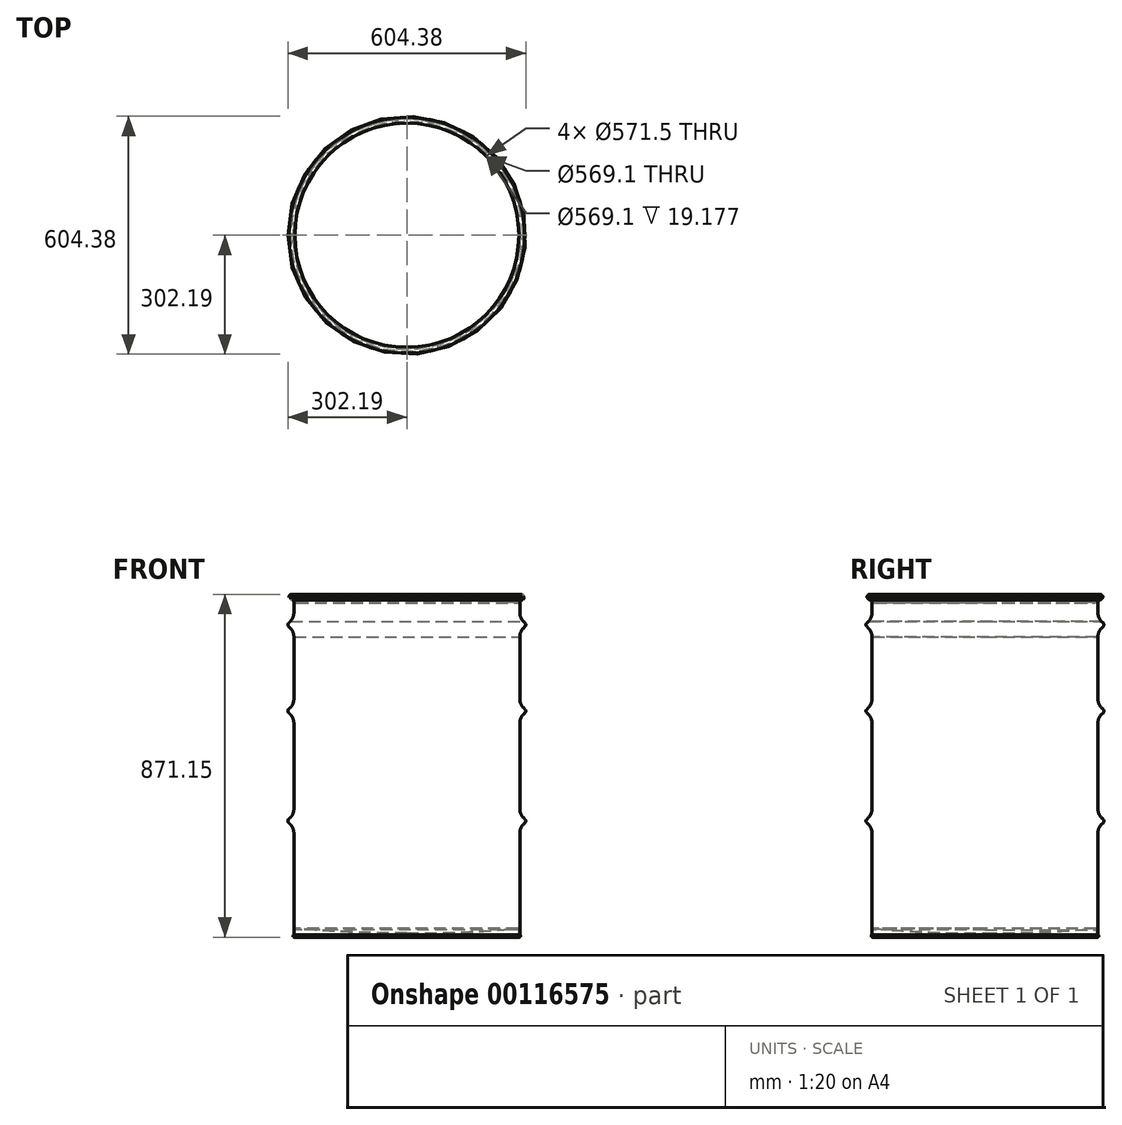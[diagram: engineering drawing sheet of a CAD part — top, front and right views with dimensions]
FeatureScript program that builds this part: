
annotation { "Feature Type Name" : "Feature", "Feature Type Description" : "" }
export const myFeature = defineFeature(function(context is Context, id is Id, definition is map)
    precondition{}
    {
        {
            var Q0;
            Q0=qCreatedBy(makeId("Front.planeOp"),FACE);
            var sketch = newSketch(context, id + "F0", { "sketchPlane" : qUnion([Q0])});
            skLineSegment(sketch, "E0.top", {"start": v(-286.95, 863.6) * mm, "end": v(-285.75, 863.6) * mm, "construction": true});
            skLineSegment(sketch, "E0.right", {"start": v(-285.75, 0) * mm, "end": v(-285.75, 264.7) * mm});
            skLineSegment(sketch, "E1", {"start": v(0, 0) * mm, "end": v(0, 177.34) * mm, "construction": true});
            skArc(sketch, "E2", {"start": v(-285.75, 863.6) * mm, "mid": v(-297.8, 866.42) * mm, "end": v(-288.25, 858.55) * mm});
            skArc(sketch, "E3", {"start": v(-286.95, 863.6) * mm, "mid": v(-296.72, 865.89) * mm, "end": v(-288.98, 859.5) * mm});
            skLineSegment(sketch, "E4", {"start": v(-288.98, 859.5) * mm, "end": v(-288.25, 858.55) * mm});
            skArc(sketch, "E5", {"start": v(-285.75, 0) * mm, "mid": v(-288.87, 2.56) * mm, "end": v(-286.95, 6.11) * mm});
            skLineSegment(sketch, "E6.trimOffspring", {"start": v(-286.95, 6.11) * mm, "end": v(-286.95, 264.7) * mm});
            skPoint(sketch, "E0.left.start.orphan", {"position": v(-286.95, 0) * mm});
            skLineSegment(sketch, "E7", {"start": v(-295.84, 802.73) * mm, "end": v(-300.33, 798.24) * mm});
            skLineSegment(sketch, "E8", {"start": v(-300.33, 789.26) * mm, "end": v(-295.84, 784.77) * mm});
            skLineSegment(sketch, "E9.trimOffspring", {"start": v(-286.95, 824.2) * mm, "end": v(-286.95, 863.6) * mm});
            skArc(sketch, "E10.filletArc", {"start": v(-300.33, 798.24) * mm, "mid": v(-302.2, 793.75) * mm, "end": v(-300.33, 789.26) * mm});
            skArc(sketch, "E11.filletArc", {"start": v(-295.84, 802.73) * mm, "mid": v(-289.26, 812.58) * mm, "end": v(-286.95, 824.2) * mm});
            skArc(sketch, "E12.filletArc", {"start": v(-286.95, 763.3) * mm, "mid": v(-289.26, 774.92) * mm, "end": v(-295.84, 784.77) * mm});
            skLineSegment(sketch, "E13", {"start": v(-302.19, 748.51) * mm, "end": v(-302.19, 170.1) * mm, "construction": true});
            skLineSegment(sketch, "E14", {"start": v(-292.1, 863.6) * mm, "end": v(-292.1, 869.95) * mm, "construction": true});
            skLineSegment(sketch, "E15", {"start": v(-300.33, 798.24) * mm, "end": v(-300.33, 789.26) * mm, "construction": true});
            skLineSegment(sketch, "E16", {"start": v(-295.84, 802.73) * mm, "end": v(-295.84, 784.77) * mm, "construction": true});
            skLineSegment(sketch, "E17", {"start": v(-286.95, 763.3) * mm, "end": v(-285.75, 763.3) * mm, "construction": true});
            skLineSegment(sketch, "E18", {"start": v(-286.95, 824.2) * mm, "end": v(-285.75, 824.2) * mm, "construction": true});
            skLineSegment(sketch, "E19.trimOffspring", {"start": v(-285.75, 824.2) * mm, "end": v(-285.75, 863.6) * mm});
            skLineSegment(sketch, "E20", {"start": v(-299.35, 790.24) * mm, "end": v(-294.86, 785.75) * mm});
            skLineSegment(sketch, "E21", {"start": v(-299.35, 797.26) * mm, "end": v(-294.86, 801.75) * mm});
            skArc(sketch, "E22", {"start": v(-299.35, 797.26) * mm, "mid": v(-300.8, 793.75) * mm, "end": v(-299.35, 790.24) * mm});
            skArc(sketch, "E23", {"start": v(-294.86, 801.75) * mm, "mid": v(-288.12, 812.08) * mm, "end": v(-285.75, 824.2) * mm});
            skArc(sketch, "E24", {"start": v(-285.75, 763.3) * mm, "mid": v(-288.03, 775.45) * mm, "end": v(-294.86, 785.75) * mm});
            skLineSegment(sketch, "E25", {"start": v(-295.84, 583.53) * mm, "end": v(-300.33, 579.04) * mm});
            skLineSegment(sketch, "E26", {"start": v(-300.33, 570.06) * mm, "end": v(-295.84, 565.57) * mm});
            skLineSegment(sketch, "E27.trimOffspring", {"start": v(-286.95, 605) * mm, "end": v(-286.95, 763.3) * mm});
            skPoint(sketch, "E28.visualSharp", {"position": v(-304.82, 574.55) * mm});
            skArc(sketch, "E28.filletArc", {"start": v(-300.33, 579.04) * mm, "mid": v(-302.2, 574.55) * mm, "end": v(-300.33, 570.06) * mm});
            skArc(sketch, "E29.filletArc", {"start": v(-295.84, 583.53) * mm, "mid": v(-289.26, 593.38) * mm, "end": v(-286.95, 605) * mm});
            skArc(sketch, "E30.filletArc", {"start": v(-286.95, 544.1) * mm, "mid": v(-289.26, 555.72) * mm, "end": v(-295.84, 565.57) * mm});
            skLineSegment(sketch, "E31", {"start": v(-295.84, 583.53) * mm, "end": v(-295.84, 565.57) * mm, "construction": true});
            skLineSegment(sketch, "E32", {"start": v(-286.95, 544.1) * mm, "end": v(-285.75, 544.1) * mm, "construction": true});
            skLineSegment(sketch, "E33", {"start": v(-286.95, 605) * mm, "end": v(-285.75, 605) * mm, "construction": true});
            skLineSegment(sketch, "E34.trimOffspring", {"start": v(-285.75, 605) * mm, "end": v(-285.75, 763.3) * mm});
            skLineSegment(sketch, "E35", {"start": v(-299.48, 578.19) * mm, "end": v(-295, 582.68) * mm});
            skArc(sketch, "E36", {"start": v(-295, 582.68) * mm, "mid": v(-288.15, 592.92) * mm, "end": v(-285.75, 605) * mm});
            skLineSegment(sketch, "E37", {"start": v(-299.48, 570.9) * mm, "end": v(-295, 566.42) * mm});
            skArc(sketch, "E38", {"start": v(-285.75, 544.1) * mm, "mid": v(-288.15, 556.18) * mm, "end": v(-295, 566.42) * mm});
            skArc(sketch, "E39", {"start": v(-299.48, 578.19) * mm, "mid": v(-301, 574.55) * mm, "end": v(-299.48, 570.9) * mm});
            skLineSegment(sketch, "E40", {"start": v(-295.84, 304.13) * mm, "end": v(-300.33, 299.64) * mm});
            skLineSegment(sketch, "E41", {"start": v(-300.33, 290.66) * mm, "end": v(-295.84, 286.17) * mm});
            skArc(sketch, "E42.filletArc", {"start": v(-300.33, 299.64) * mm, "mid": v(-302.19, 295.15) * mm, "end": v(-300.33, 290.66) * mm});
            skLineSegment(sketch, "E43.trimOffspring", {"start": v(-286.95, 325.6) * mm, "end": v(-286.95, 544.1) * mm});
            skArc(sketch, "E44.filletArc", {"start": v(-295.84, 304.13) * mm, "mid": v(-289.26, 313.98) * mm, "end": v(-286.95, 325.6) * mm});
            skArc(sketch, "E45.filletArc", {"start": v(-286.95, 264.7) * mm, "mid": v(-289.26, 276.32) * mm, "end": v(-295.84, 286.17) * mm});
            skLineSegment(sketch, "E46", {"start": v(-300.33, 299.64) * mm, "end": v(-300.33, 290.66) * mm, "construction": true});
            skLineSegment(sketch, "E47", {"start": v(-295.84, 304.13) * mm, "end": v(-295.84, 286.17) * mm, "construction": true});
            skLineSegment(sketch, "E48", {"start": v(-286.95, 325.6) * mm, "end": v(-285.75, 325.6) * mm, "construction": true});
            skLineSegment(sketch, "E49", {"start": v(-286.95, 264.7) * mm, "end": v(-285.75, 264.7) * mm, "construction": true});
            skLineSegment(sketch, "E50.trimOffspring", {"start": v(-285.75, 325.6) * mm, "end": v(-285.75, 544.1) * mm});
            skLineSegment(sketch, "E51", {"start": v(-299.48, 298.79) * mm, "end": v(-295, 303.28) * mm});
            skLineSegment(sketch, "E52", {"start": v(-299.48, 291.5) * mm, "end": v(-295, 287.02) * mm});
            skArc(sketch, "E53", {"start": v(-295, 303.28) * mm, "mid": v(-288.15, 313.52) * mm, "end": v(-285.75, 325.6) * mm});
            skArc(sketch, "E54", {"start": v(-285.75, 264.7) * mm, "mid": v(-288.15, 276.78) * mm, "end": v(-295, 287.02) * mm});
            skArc(sketch, "E55", {"start": v(-299.48, 298.79) * mm, "mid": v(-300.99, 295.15) * mm, "end": v(-299.48, 291.5) * mm});
            skSolve(sketch);
        }
        {
            var Q0;
            Q0 = qSketchRegion(id + "F0", true);
            var Q1;
            Q1 = qConstructionFilter(qBodyType(qCreatedBy(id + "F0" ,EDGE), BodyType.WIRE), ConstructionObject.NO);
            var Q2;
            Q2=sQuery(id+"F0.wireOp",EDGE,"E1");
            revolve(context, id + "F1", {"entities" : qUnion([Q0]), "surfaceEntities" : qUnion([Q1]), "axis" : qUnion([Q2]), "revolveType" : RevolveType.FULL});
        }
        {
            var Q0;
            Q0=qCreatedBy(makeId("Front.planeOp"),FACE);
            var sketch = newSketch(context, id + "F2", { "sketchPlane" : qUnion([Q0])});
            skLineSegment(sketch, "E56", {"start": v(286.95, 6.11) * mm, "end": v(286.95, 264.7) * mm});
            skArc(sketch, "E57", {"start": v(285.75, 0) * mm, "mid": v(288.87, 2.56) * mm, "end": v(286.95, 6.11) * mm});
            skLineSegment(sketch, "E58", {"start": v(285.75, 0) * mm, "end": v(285.75, 264.7) * mm});
            skLineSegment(sketch, "E59", {"start": v(-285.75, 264.7) * mm, "end": v(-285.75, 0) * mm});
            skLineSegment(sketch, "E60", {"start": v(-285.75, 0) * mm, "end": v(-284.55, 0) * mm});
            skLineSegment(sketch, "E61", {"start": v(-284.55, 0) * mm, "end": v(-284.55, 19.18) * mm});
            skArc(sketch, "E62", {"start": v(-282.4, 21.14) * mm, "mid": v(-283.91, 20.63) * mm, "end": v(-284.55, 19.18) * mm});
            skLineSegment(sketch, "E63", {"start": v(0, 244.83) * mm, "end": v(0, -50.53) * mm, "construction": true});
            skArc(sketch, "E64", {"start": v(-282.4, 21.14) * mm, "mid": v(-141.33, 12.15) * mm, "end": v(0, 9.14) * mm});
            skLineSegment(sketch, "E65", {"start": v(0, 9.14) * mm, "end": v(0, 10.34) * mm});
            skArc(sketch, "E66", {"start": v(-285.75, 19.18) * mm, "mid": v(-284.72, 21.52) * mm, "end": v(-282.3, 22.34) * mm});
            skArc(sketch, "E67", {"start": v(-282.3, 22.34) * mm, "mid": v(-141.28, 13.34) * mm, "end": v(0, 10.34) * mm});
            skLineSegment(sketch, "E68", {"start": v(-282.58, 19.18) * mm, "end": v(-282.58, 22.35) * mm, "construction": true});
            skSolve(sketch);
        }
        {
            var Q0;
            Q0 = qSketchRegion(id + "F2", true);
            var Q1;
            Q1=sQuery(id+"F2.wireOp",EDGE,"E63");
            revolve(context, id + "F3", {"operationType" : NewBodyOperationType.ADD, "entities" : qUnion([Q0]), "axis" : qUnion([Q1]), "revolveType" : RevolveType.FULL});
        }
        {
            var Q0;
            Q0=qCreatedBy(makeId("Front.planeOp"),FACE);
            var sketch = newSketch(context, id + "F4", { "sketchPlane" : qUnion([Q0])});
            skLineSegment(sketch, "E69", {"start": v(0, 998.16) * mm, "end": v(0, -198.69) * mm, "construction": true});
            skArc(sketch, "E70", {"start": v(-288.25, 858.55) * mm, "mid": v(-297.8, 866.42) * mm, "end": v(-285.75, 863.6) * mm, "construction": true});
            skLineSegment(sketch, "E71", {"start": v(-285.75, 863.6) * mm, "end": v(-285.75, 824.2) * mm, "construction": true});
            skArc(sketch, "E72", {"start": v(-298.45, 863.6) * mm, "mid": v(-292.1, 869.95) * mm, "end": v(-285.75, 863.6) * mm});
            skLineSegment(sketch, "E73", {"start": v(-285.75, 863.6) * mm, "end": v(-285.75, 855.15) * mm});
            skArc(sketch, "E74", {"start": v(-285.75, 855.15) * mm, "mid": v(-283.75, 850.52) * mm, "end": v(-279.02, 848.8) * mm});
            skArc(sketch, "E75", {"start": v(-279.02, 848.8) * mm, "mid": v(-139.57, 855.14) * mm, "end": v(0, 857.25) * mm});
            skLineSegment(sketch, "E76", {"start": v(-298.45, 863.6) * mm, "end": v(-299.65, 863.6) * mm});
            skArc(sketch, "E77", {"start": v(-299.65, 863.6) * mm, "mid": v(-292.1, 871.15) * mm, "end": v(-284.55, 863.6) * mm});
            skLineSegment(sketch, "E78", {"start": v(-284.55, 863.6) * mm, "end": v(-284.55, 855.15) * mm});
            skArc(sketch, "E79", {"start": v(-284.55, 855.15) * mm, "mid": v(-282.93, 851.4) * mm, "end": v(-279.09, 850) * mm});
            skArc(sketch, "E80", {"start": v(-279.09, 850) * mm, "mid": v(-139.6, 856.34) * mm, "end": v(0, 858.45) * mm});
            skLineSegment(sketch, "E81", {"start": v(0, 858.45) * mm, "end": v(0, 857.25) * mm});
            skLineSegment(sketch, "E82", {"start": v(-279.4, 855.15) * mm, "end": v(-279.02, 848.8) * mm, "construction": true});
            skLineSegment(sketch, "E83", {"start": v(-279.4, 855.15) * mm, "end": v(-279.4, 848.8) * mm, "construction": true});
            skLineSegment(sketch, "E84", {"start": v(-292.1, 863.6) * mm, "end": v(-292.1, 871.15) * mm, "construction": true});
            skSolve(sketch);
        }
        {
            var Q0;
            Q0 = qSketchRegion(id + "F4", true);
            var Q1;
            Q1=sQuery(id+"F4.wireOp",EDGE,"E69");
            revolve(context, id + "F5", {"entities" : qUnion([Q0]), "axis" : qUnion([Q1]), "revolveType" : RevolveType.FULL});
        }
    });
